# Revit family: Doors_Sliding_Avanti_Systems_Cloud-Assisted-Close-Premium-Sliding-Glass-Door_Soffit-Mount-Dbl-Glazed
name_source: partatom
category: Doors
revit_build: Autodesk Revit Architecture 2015 (Build: 20140606_1530(x64)
units: mm (PartAtom-declared; Revit-internal decimal feet)

## types (1)
- Load Family Type Catalog
    Analytic Construction = <None>
    BIMobject category = Sliding
    BIMobject category code = doors-sliding
    BIMobject main category = Doors
    BIMobject main category code = doors
    Brand url = http://www.avantisystemsusa.com
    Clear Anodic Finish = AAMA 611, AA-M12c22A31, Class II, 0.01mm or thicker
    Description = Premium automated interior sliding glass door which can be integrated int the Solare Single Glazed, Solare Double Glazed, Elite Frree standing and a solid traditional wall.
    Design country = United States
    Edition number = 1
    Function = Interior
    Gap Thickness = 1/2"
    Glass Marker = Yes
    Glass Material = Glass - Avanti -  Low Iron
    Glazing = Safety Glazing SGCC
    IFC Classification = Door
    LEED compatibility = YES
    Ladder Pull Height = 18"
    Lock = Thumb turn floor lock with a key
    Manufacturer = Avanti Systems USA
    Manufacturer name = Avanti Systems
    Masterformat 2014 Code = 08 32 13
    Masterformat 2014 Description = Sliding Aluminum-Framed Glass Doors
    Material main = Glass
    Material secondary = Aluminium
    Model = Cloud ™ Assisted Close Premium Sliding Glass Door
    NBS Reference Code = 59-23-77
    NBS Reference Description = Sliding Door And Partition Sets
    Nominal height = 0"
    Nominal width = 0"
    OmniClass Code = 23-17 11 23 13
    OmniClass Description = Sliding All Glass Doors
    Product Guid = 9d9dc9e6-079c-47eb-8ec1-d69015d0589f
    Product SKU = avanti-cloud-assisted-close
    Product data url = https://bimobject.com
    Product family = Sliding Doors
    Product group = Assisted Close
    Product url = https://www.avantisystemsusa.com
    QR code = http://bimobject.com
    Sound Rating = 0
    Thickness = 1/2"
    Type = 3
    UNSPSC Code = 30171501
    URL = https://www.avantisystemsusa.com
    Uniclass 1.4 Code = JL20
    Uniclass 1.4 Description = Doors
    Uniclass 2.0 Code = PR-59-23-77
    Uniclass 2.0 Description = Sliding Door And Partition Sets
    Uniclass 2015 Code = Pr_30_59_24_80
    Uniclass 2015 Name = Sliding door and partition sets
    Uniformat II Code = C1020
    Uniformat II Description = Interior Doors
    Warranty = 1 year
    Weight Net (Kg) = 0

## geometry (parser evidence)
native form markers: Sweep x29
no freeform markers — native parametric forms only
